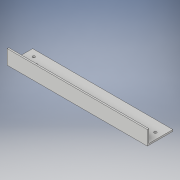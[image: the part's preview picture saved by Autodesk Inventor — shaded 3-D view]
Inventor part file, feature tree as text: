
AUTODESK INVENTOR PART (.ipt)
format: ipt  version: 2018 (Build 220112000, 112)  size: 121,856 bytes
history: native  units: in
note: dims shown in document units (in); Inventor stores cm internally (conversion verified against a paired STEP export)
features: extrude x4, sketch x4
ambient origin geometry x8: Origin, YZ Plane, XZ Plane, XY Plane, X Axis, Y Axis, Z Axis, Center Point
bodies: Solid1 (feature_tree)
feature tree (8):
  extrude  "Extrusion1"  Depth=2.0in
  extrude  "Extrusion2"  Depth=11.0in
  extrude  "Extrusion3"  Depth=1.0in TaperAngle=0.0deg
  extrude  "Extrusion4"  Depth=1.0in
  sketch  "Sketch1"  dims[d0=11.0in d1=2.0in]
  sketch  "Sketch2"  dims[d2=0.125in d3=0.0in d4=11.0in]
  sketch  "Sketch3"  dims[d5=0.125in d6=1.0in d7=0.0in]
  sketch  "Sketch4"  dims[d14=1.0in d15=0.0in d26=0.5in d27=0.875in d28=0.2031in d29=1.0in d30=0.0in]
